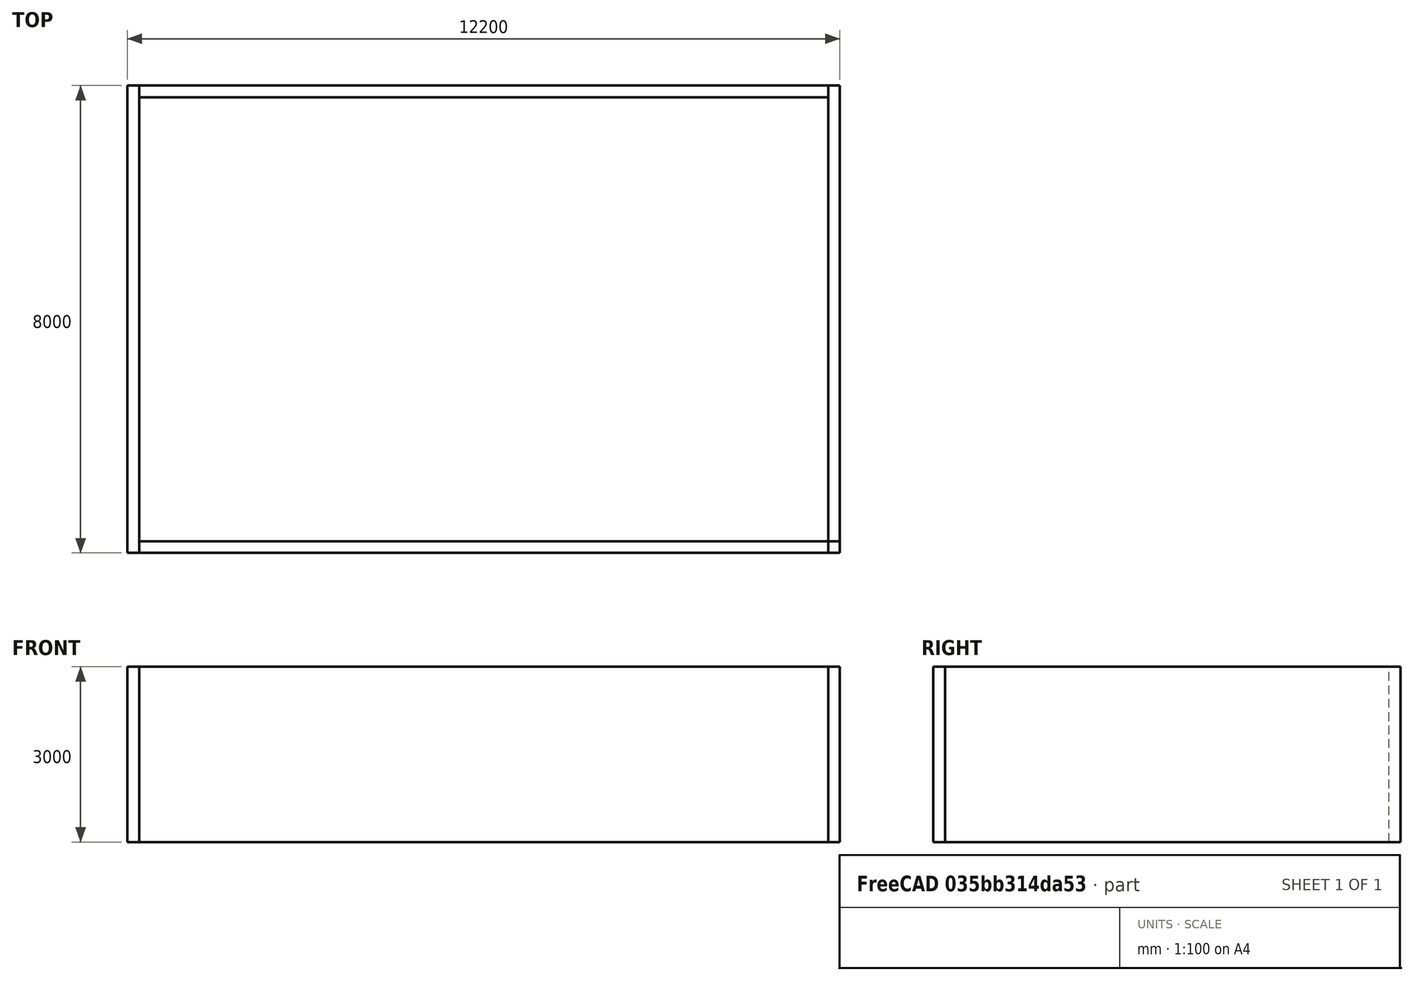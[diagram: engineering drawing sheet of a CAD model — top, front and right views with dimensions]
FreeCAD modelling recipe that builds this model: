
FCSTD DOCUMENT  (FreeCAD 1.0R39319 (Git))
Label: Unnamed2
License: All rights reserved
LicenseURL: http://en.wikipedia.org/wiki/All_rights_reserved
objects: Part::Part2DObjectPython×4, Part::FeaturePython×4, App::DocumentObjectGroup×1
note: 8 computed .brp shape members not serialized (recipe doc carries the construction recipe); baked Part::Feature solids carry a one-line shape summary decoded from their .brp

FEATURE [Part::Part2DObjectPython] Line  # Draft 2D object (typed FeaturePython)
  Area = 0
  ChamferSize = 0
  Closed = false
  End = (0,0,0)
  FilletRadius = 0
  Length = 12000
  MakeFace = true
  Placement = pos=(12000,0,0) rot=(0,0,1;0rad)
  Points = (2) [(0,0,0),(-12000,0,0)]
  Start = (12000,0,0)
  Subdivisions = 0
FEATURE [Part::Part2DObjectPython] Line001  # Draft 2D object (typed FeaturePython)
  Area = 0
  ChamferSize = 0
  Closed = false
  End = (0,0,0)
  FilletRadius = 0
  Length = 8000
  MakeFace = true
  Placement = pos=(0,8000,0) rot=(0,0,1;0rad)
  Points = (2) [(0,0,0),(0,-8000,0)]
  Start = (0,8000,0)
  Subdivisions = 0
FEATURE [Part::Part2DObjectPython] Line002  # Draft 2D object (typed FeaturePython)
  Area = 0
  ChamferSize = 0
  Closed = false
  End = (12000,8000,0)
  FilletRadius = 0
  Length = 12000
  MakeFace = true
  Placement = pos=(0,8000,0) rot=(0,0,1;0rad)
  Points = (2) [(0,0,0),(12000,0,0)]
  Start = (0,8000,0)
  Subdivisions = 0
FEATURE [Part::Part2DObjectPython] Line003  # Draft 2D object (typed FeaturePython)
  Area = 0
  ChamferSize = 0
  Closed = false
  End = (12000,0,0)
  FilletRadius = 0
  Length = 8000
  MakeFace = true
  Placement = pos=(12000,8000,0) rot=(0,0,1;0rad)
  Points = (2) [(0,0,0),(0,-8000,0)]
  Start = (12000,8000,0)
  Subdivisions = 0
FEATURE [App::DocumentObjectGroup] Group
  Group = -> [Line003,Line,Line001,Line002]
FEATURE [Part::FeaturePython] Wall  # Arch/BIM 166 (typed FeaturePython)
  Align = 0
  ArchSketchData = true
  Area = 24000000
  Base = -> Line003
  BlockHeight = 0
  BlockLength = 0
  CountBroken = 0
  CountEntire = 0
  Face = 0
  Height = 3000
  HorizontalArea = 1600000
  IfcData = attributes={"GlobalId": {"name": "GlobalId", "type": "IfcGloballyUniqueId", "is_enum": false, "enum_values": []}, "Description": {"... (+533 chars omitted),+1 more (map truncated)
  IfcType = 166
  Joint = 0
  Length = 8000
  MakeBlocks = false
  MoveBase = false
  MoveWithHost = false
  Normal = (0,0,0)
  OffsetFirst = 0
  OffsetSecond = 0
  PerimeterLength = 16400
  PredefinedType = 0
  VerticalArea = 4.92e+07
  Width = 200
FEATURE [Part::FeaturePython] Wall001  # Arch/BIM 166 (typed FeaturePython)
  Align = 0
  ArchSketchData = true
  Area = 36000000
  Base = -> Line
  BlockHeight = 0
  BlockLength = 0
  CountBroken = 0
  CountEntire = 0
  Face = 0
  Height = 3000
  HorizontalArea = 2400000
  IfcData = attributes={"GlobalId": {"name": "GlobalId", "type": "IfcGloballyUniqueId", "is_enum": false, "enum_values": []}, "Description": {"... (+533 chars omitted),+1 more (map truncated)
  IfcType = 166
  Joint = 0
  Length = 12000
  MakeBlocks = false
  MoveBase = false
  MoveWithHost = false
  Normal = (0,0,0)
  OffsetFirst = 0
  OffsetSecond = 0
  PerimeterLength = 24400
  PredefinedType = 0
  VerticalArea = 73200000
  Width = 200
FEATURE [Part::FeaturePython] Wall002  # Arch/BIM 166 (typed FeaturePython)
  Align = 0
  ArchSketchData = true
  Area = 24000000
  Base = -> Line001
  BlockHeight = 0
  BlockLength = 0
  CountBroken = 0
  CountEntire = 0
  Face = 0
  Height = 3000
  HorizontalArea = 1600000
  IfcData = attributes={"GlobalId": {"name": "GlobalId", "type": "IfcGloballyUniqueId", "is_enum": false, "enum_values": []}, "Description": {"... (+533 chars omitted),+1 more (map truncated)
  IfcType = 166
  Joint = 0
  Length = 8000
  MakeBlocks = false
  MoveBase = false
  MoveWithHost = false
  Normal = (0,0,0)
  OffsetFirst = 0
  OffsetSecond = 0
  PerimeterLength = 16400
  PredefinedType = 0
  VerticalArea = 4.92e+07
  Width = 200
FEATURE [Part::FeaturePython] Wall003  # Arch/BIM 166 (typed FeaturePython)
  Additions = -> [Wall,Wall001,Wall002]
  Align = 0
  ArchSketchData = true
  Area = 36000000
  Base = -> Line002
  BlockHeight = 0
  BlockLength = 0
  CountBroken = 0
  CountEntire = 0
  Face = 0
  Height = 3000
  HorizontalArea = 7920000
  IfcData = attributes={"GlobalId": {"name": "GlobalId", "type": "IfcGloballyUniqueId", "is_enum": false, "enum_values": []}, "Description": {"... (+533 chars omitted),+1 more (map truncated)
  IfcType = 166
  Joint = 0
  Length = 12000
  MakeBlocks = false
  MoveBase = false
  MoveWithHost = false
  Normal = (0,0,0)
  OffsetFirst = 0
  OffsetSecond = 0
  PerimeterLength = 79200
  PredefinedType = 0
  VerticalArea = 237600000
  Width = 200
